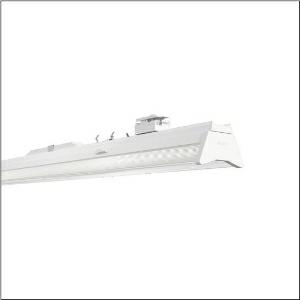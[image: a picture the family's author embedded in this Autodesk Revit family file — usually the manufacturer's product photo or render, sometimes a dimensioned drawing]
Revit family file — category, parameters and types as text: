
# Revit family: licross_21_performance_mo_52td16dn46xg
name_source: partatom
category: Lighting Fixtures
units: mm (PartAtom-declared; Revit-internal decimal feet)

## family parameters
Cut with Voids When Loaded = No
Host = Face
Light Source = No
Part Type = Normal
Room Calculation Point = No
Round Connector Dimension = Use Diameter
Shared = No

## types (1)
- --- (1 x LED, 6000 lm, 32.7 W, 4000K)
    Apparent Load = 33 VA
    CIE Flux Codes = 66 88 96 79 100
    Color Rendering = 80
    Color Temperature = 4000K
    Default Elevation = 1800 mm
    Description = Licross 21 Performance MO, luminaire insert, of sheet steel, galvanised, coil coated, white, length: 1.500mm, width: 120mm, height: 123mm, LED rated luminous flux: 6.000lm, light colour: 840, SDCM (Standard Deviation of Colour Matching)MacAdam ≤ 3 SDCM (initial), control gear: DALI 2, with plug, 5-pole, with phase selection, mains connection: 220..240V, AC, 50/60Hz, rated input power: 33W, internal wiring halogen-free, primary light control with lens, of plastic, primary optical cover: cover, of PMMA, light emission: direct/indirect distribution, primary light characteristic: symmetric, protection rating (complete): IP54, insulation class (complete): insulation class I (protective earthing), certification: CE, ENEC, VDE, UKCA, protection symbol: D if used in an environment with non-conductive dust loads with corresponding accessories, impact resistance: IK06, permissible ambient temperature for indoor applications: -25..+45°C, corresponds to IFS (International Featured Standards) requirements for safety and quality in the food industry, reducing of maximum allowable ambient temperature of 5°C with ceiling mounting, LABS conformity tested according to VDMA 24364:2018-05, The light source and the operating device comply with the requirements of the Ecodesign Regulation (EU) 2019/2020 and are replaceable in accordance with this regulation, packaging unit: 1 piece
    Height = 114 mm
    Lamp = 1 x LED
    Lamp Light Flux = 6000 lm
    Lamp Power = 32.7 W
    Lamp count = 1
    Length = 1500 mm
    Luminous efficacy = 183 lm/W
    Manufacturer = Siteco
    ModVariant = No
    Model = 52TD16DN46XG
    Mounting Place = Ceiling
    Mounting Type = Pendant
    Number of Poles = 1
    OnlyDefault = Yes
    Power Factor = 1
    Product Name = Licross 21 Performance MO
    Product group = luminaire insert | ceiling pendant
    ProductGroupID = 901
    Protection Class = Protection class I
    Protection Degree = IP 54
    RLX_Detail_Level = 1
    RLX_Emergency_Light_Flux = 0 lm
    RLX_Emergency_Type = 0
    RLX_Emergency_Type_DB = No
    RlxData = <blob elided: 34061 chars, md5=e2d4f3fe>
    Socket = socket
    Standby Power = 0 W
    System Light Flux = 6000 lm
    System Power = 33 W
    Type Comments = factory setting: luminous flux: 100 % | dim-lin: 254 | 222 mA
    Type Image = l_1256138.jpg
    URL = http://relux.com
    VarID = @adj_129355
    Voltage = 0 V
    Weight = 0.00 kg
    Width = 120 mm

## geometry (parser evidence)
native form markers: Blend x4, Sweep x14
no freeform markers — native parametric forms only
